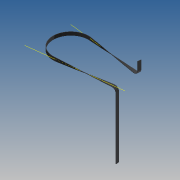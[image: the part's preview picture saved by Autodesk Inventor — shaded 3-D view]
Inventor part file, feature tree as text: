
AUTODESK INVENTOR PART (.ipt)
format: ipt  version: 2013 (Build 170138000, 138)  size: 165,376 bytes
history: native  units: mm
features: sketch x8, extrude x4, other x2, helix x2, revolve x2, reference x2
ambient origin geometry x8: Origin, YZ Plane, XZ Plane, XY Plane, X Axis, Y Axis, Z Axis, Center Point
bodies: Solid1 (feature_tree)
feature tree (20):
  extrude  "Extrusion1"  Depth=0.254mm
  extrude  "Extrusion2"  Depth=6.0mm TaperAngle=0.0deg
  sketch  "Sketch3"  dims[d9=0.254mm]
  other  "Work Axis1"
  helix  "Coil1"  [1 undecoded]
  sketch  "Sketch4"  dims[d10=91.864mm d11=92.864mm d12=2.5mm d13=0.0mm d14=90.0deg d15=90.0deg d16=0.0mm d17=0.0mm d18=0.254mm]
  other  "Work Axis2"
  helix  "Coil2"  [1 undecoded]
  revolve  "Revolution1"  [1 undecoded]
  revolve  "Revolution2"  [1 undecoded]
  extrude  "Extrusion5"  Depth=7.0mm
  extrude  "Extrusion4"  Depth=10.0mm TaperAngle=0.0deg
  sketch  "Sketch1"  dims[d0=63.661977mm d2=0.254mm]
  sketch  "Sketch2"  dims[d3=0.375mm d4=6.0mm d5=0.0mm d6=29.040533mm d7=0.0mm d8=0.0mm]
  sketch  "Sketch5"  dims[d19=91.864mm d20=92.864mm d21=2.5mm d22=0.0mm d23=90.0deg d24=90.0deg d25=0.0mm d26=0.0mm d27=7.0mm]
  sketch  "Sketch6"  dims[d28=90.0deg d29=7.0mm]
  sketch  "Sketch8"  dims[d30=90.0deg d34=10.0mm d35=0.0mm]
  reference  "Reference1"
  sketch  "Sketch9"  dims[d36=10.0mm d37=0.0mm]
  reference  "Reference2"
note: 4 required parameter values undecoded (feature->parameter linkage not recoverable at this tier; creation-order binding heuristic only, values carry confidence <= 0.55)